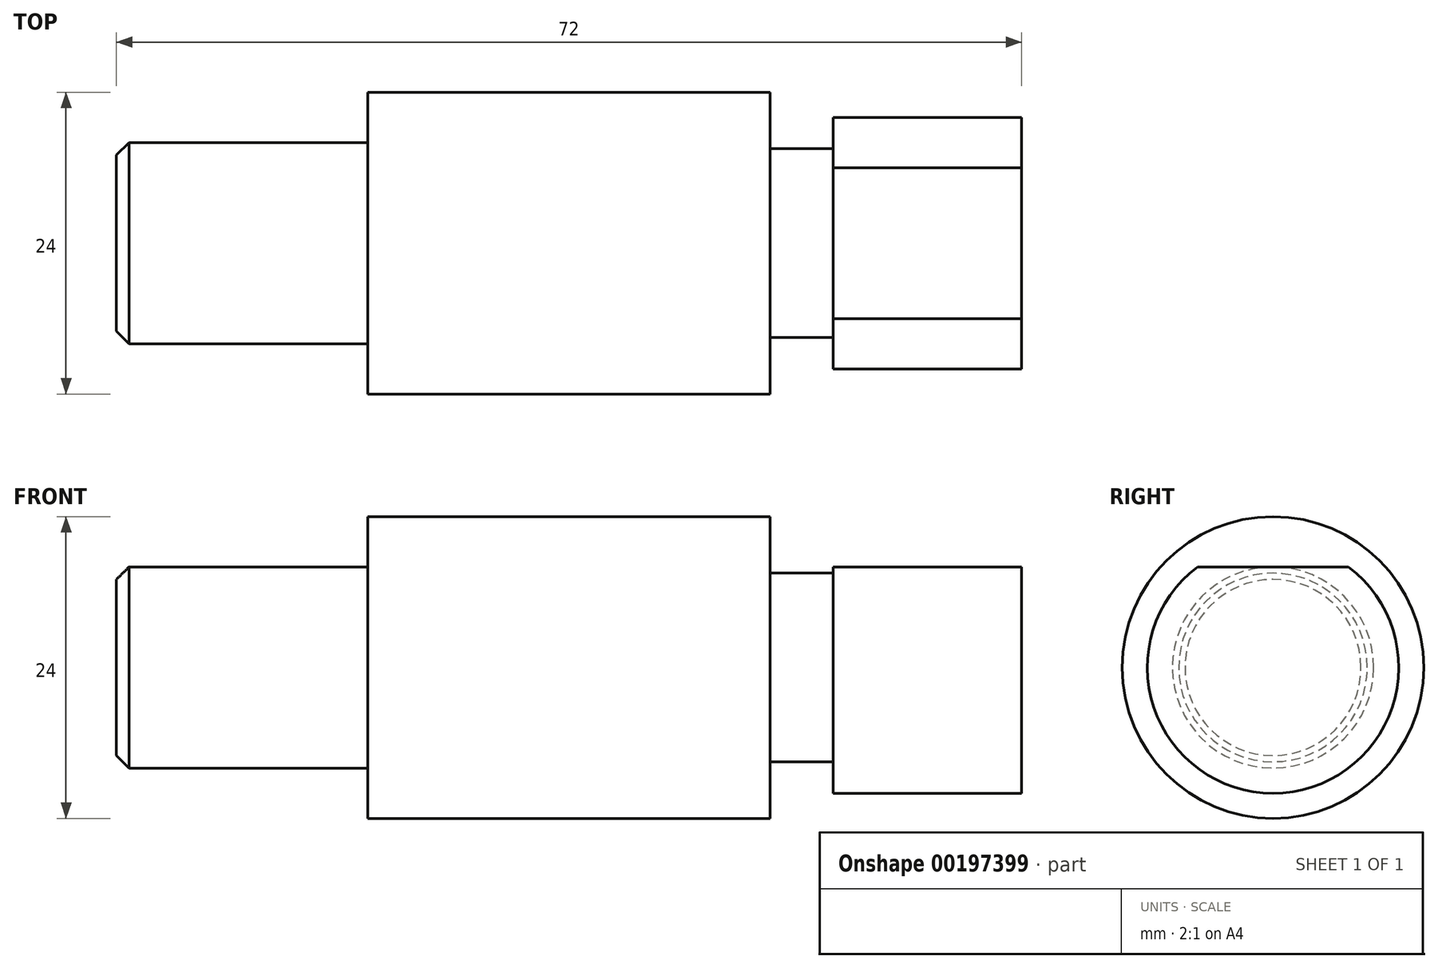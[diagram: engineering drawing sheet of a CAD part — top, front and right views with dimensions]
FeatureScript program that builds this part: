
annotation { "Feature Type Name" : "Feature", "Feature Type Description" : "" }
export const myFeature = defineFeature(function(context is Context, id is Id, definition is map)
    precondition{}
    {
        {
            var Q0;
            Q0=qCreatedBy(makeId("Front.planeOp"),FACE);
            var sketch = newSketch(context, id + "F0", { "sketchPlane" : qUnion([Q0])});
            skLineSegment(sketch, "E0", {"start": v(-6.76, 0) * mm, "end": v(72.87, 0) * mm, "construction": true});
            skLineSegment(sketch, "E1", {"start": v(0, 0) * mm, "end": v(0, 8) * mm});
            skLineSegment(sketch, "E2", {"start": v(0, 8) * mm, "end": v(20, 8) * mm});
            skLineSegment(sketch, "E3", {"start": v(20, 8) * mm, "end": v(20, 12) * mm});
            skLineSegment(sketch, "E4", {"start": v(20, 12) * mm, "end": v(52, 12) * mm});
            skLineSegment(sketch, "E5", {"start": v(52, 12) * mm, "end": v(52, 7.5) * mm});
            skLineSegment(sketch, "E6", {"start": v(52, 7.5) * mm, "end": v(57, 7.5) * mm});
            skLineSegment(sketch, "E7", {"start": v(57, 7.5) * mm, "end": v(57, 10) * mm});
            skLineSegment(sketch, "E8", {"start": v(57, 10) * mm, "end": v(72, 10) * mm});
            skLineSegment(sketch, "E9", {"start": v(72, 10) * mm, "end": v(72, 0) * mm});
            skLineSegment(sketch, "E10", {"start": v(72, 0) * mm, "end": v(0, 0) * mm});
            skSolve(sketch);
        }
        {
            var Q0;
            Q0 = qSketchRegion(id + "F0", true);
            var Q1;
            Q1=sQuery(id+"F0.wireOp",EDGE,"E0");
            revolve(context, id + "F1", {"entities" : qUnion([Q0]), "axis" : qUnion([Q1]), "revolveType" : RevolveType.FULL});
        }
        {
            var Q0;
            Q0=makeQuery(id+"F1.opRevolve","SWEPT_EDGE",EDGE,{"disambiguationData":[OSD([sQuery(id+"F0.wireOp",EDGE,"E1"),sQuery(id+"F0.wireOp",EDGE,"E2")])]});
            chamfer(context, id + "F2", {"entities" : qUnion([Q0]), "width" : 1 * mm, "tangentPropagation" : true});
        }
        {
            var Q0;
            Q0=makeQuery(id+"F1.opRevolve","SWEPT_FACE",FACE,{"disambiguationData":[OSD([sQuery(id+"F0.wireOp",EDGE,"E9")])]});
            var sketch = newSketch(context, id + "F3", { "sketchPlane" : qUnion([Q0])});
            skArc(sketch, "E11.0", {"start": v(6, 8) * mm, "mid": v(0, 10) * mm, "end": v(-6, 8) * mm});
            skLineSegment(sketch, "E12", {"start": v(-6, 8) * mm, "end": v(6, 8) * mm});
            skSolve(sketch);
        }
        {
            var Q0;
            Q0 = qSketchRegion(id + "F3", true);
            extrude(context, id + "F4", {"entities" : qUnion([Q0]), "operationType" : NewBodyOperationType.REMOVE, "oppositeDirection" : true, "depth" : 15 * mm});
        }
    });
